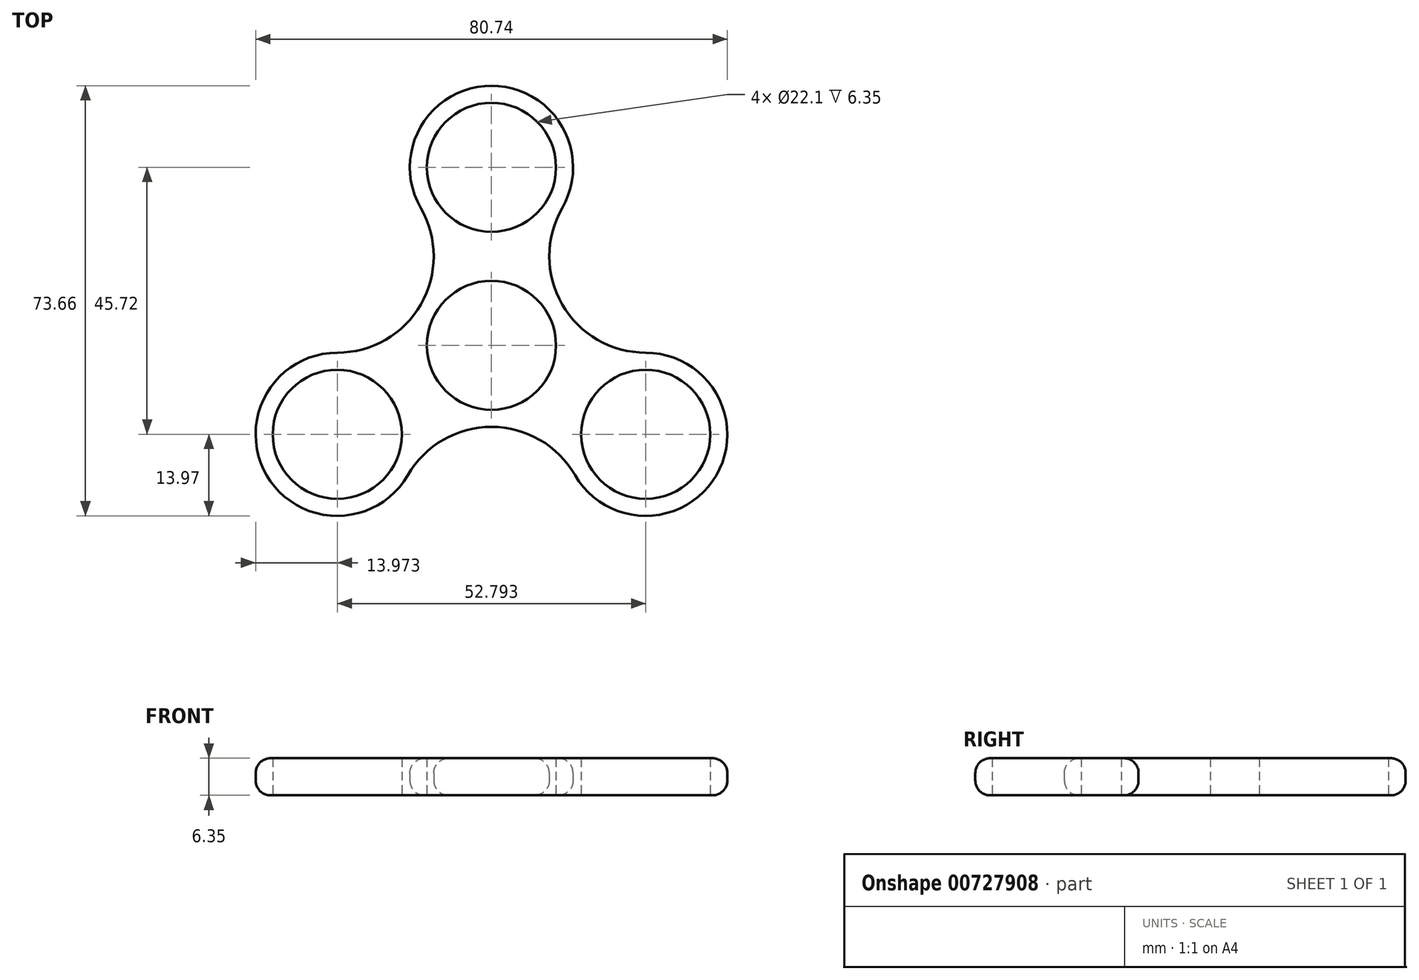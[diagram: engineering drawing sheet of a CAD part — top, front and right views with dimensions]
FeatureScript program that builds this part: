
annotation { "Feature Type Name" : "Feature", "Feature Type Description" : "" }
export const myFeature = defineFeature(function(context is Context, id is Id, definition is map)
    precondition{}
    {
        {
            var Q0;
            Q0=qCreatedBy(makeId("Top.planeOp"),FACE);
            var sketch = newSketch(context, id + "F0", { "sketchPlane" : qUnion([Q0])});
            skCircle(sketch, "E0", {"center": v(0, 0) * mm, "radius": 11.05 * mm});
            skCircle(sketch, "E1", {"center": v(0, 0) * mm, "radius": 13.97 * mm});
            skLineSegment(sketch, "E2", {"start": v(0, 0) * mm, "end": v(0, 30.48) * mm});
            skCircle(sketch, "E3", {"center": v(0, 30.48) * mm, "radius": 11.05 * mm});
            skCircle(sketch, "E4.1.1", {"center": v(-26.4, -15.24) * mm, "radius": 11.05 * mm});
            skCircle(sketch, "E4.2.1", {"center": v(26.4, -15.24) * mm, "radius": 11.05 * mm});
            skLineSegment(sketch, "E5", {"start": v(0, 0) * mm, "end": v(-26.4, 15.24) * mm});
            skArc(sketch, "E6", {"start": v(-26.4, -1.27) * mm, "mid": v(-12.1, 6.98) * mm, "end": v(-12.1, 23.5) * mm});
            skCircle(sketch, "E7", {"center": v(0, 30.48) * mm, "radius": 13.97 * mm});
            skCircle(sketch, "E8.1.0", {"center": v(-26.4, -15.24) * mm, "radius": 13.97 * mm});
            skArc(sketch, "E9.1.0", {"start": v(14.3, -22.23) * mm, "mid": v(0, -13.97) * mm, "end": v(-14.3, -22.22) * mm});
            skArc(sketch, "E9.2.0", {"start": v(12.1, 23.5) * mm, "mid": v(12.1, 6.98) * mm, "end": v(26.4, -1.27) * mm});
            skCircle(sketch, "E10", {"center": v(26.4, -15.24) * mm, "radius": 13.97 * mm});
            skPoint(sketch, "E11.orphan", {"position": v(-14.85, 27.04) * mm});
            skPoint(sketch, "E12.orphan", {"position": v(14.85, 27.04) * mm});
            skPoint(sketch, "E13.orphan", {"position": v(30.84, -0.66) * mm});
            skPoint(sketch, "E14.orphan", {"position": v(-30.84, -0.66) * mm});
            skPoint(sketch, "E15.orphan", {"position": v(-16, -26.38) * mm});
            skPoint(sketch, "E16.orphan", {"position": v(16, -26.38) * mm});
            skSolve(sketch);
        }
        {
            var Q0;
            Q0 = qSketchRegion(id + "F0", true);
            var Q1;
            {var subQ5=sQuery(id+"F0.wireOp",EDGE,"E2");var subQ7=sQuery(id+"F0.wireOp",EDGE,"E0");var subQ8=makeQuery(id+"F0.imprint","INTERSECT",VERTEX,{"derivedFrom":[subQ7,subQ5]});Q1=makeQuery(id+"F0.imprint","IMPRINT",FACE,{"disambiguationData":[TD([[makeQuery(id+"F0.imprint","IMPRINT",EDGE,{"disambiguationData":[TD([[subQ8,1.0]])],"derivedFrom":subQ7}),-1.0]])]});}
            extrude(context, id + "F1", {"entities" : qUnion([Q0, Q1]), "depth" : 6.35 * mm, "offsetDistance" : 25.4 * mm});
        }
        {
            var Q0;
            Q0=makeQuery(id+"F1.opExtrude","SWEPT_FACE",FACE,{"disambiguationData":[OSD([sQuery(id+"F0.wireOp",EDGE,"E9.2.0")])]});
            fillet(context, id + "F2", {"entities" : qUnion([Q0]), "radius" : 2.54 * mm, "tangentPropagation" : true, "allowEdgeOverflow" : false});
        }
    });
